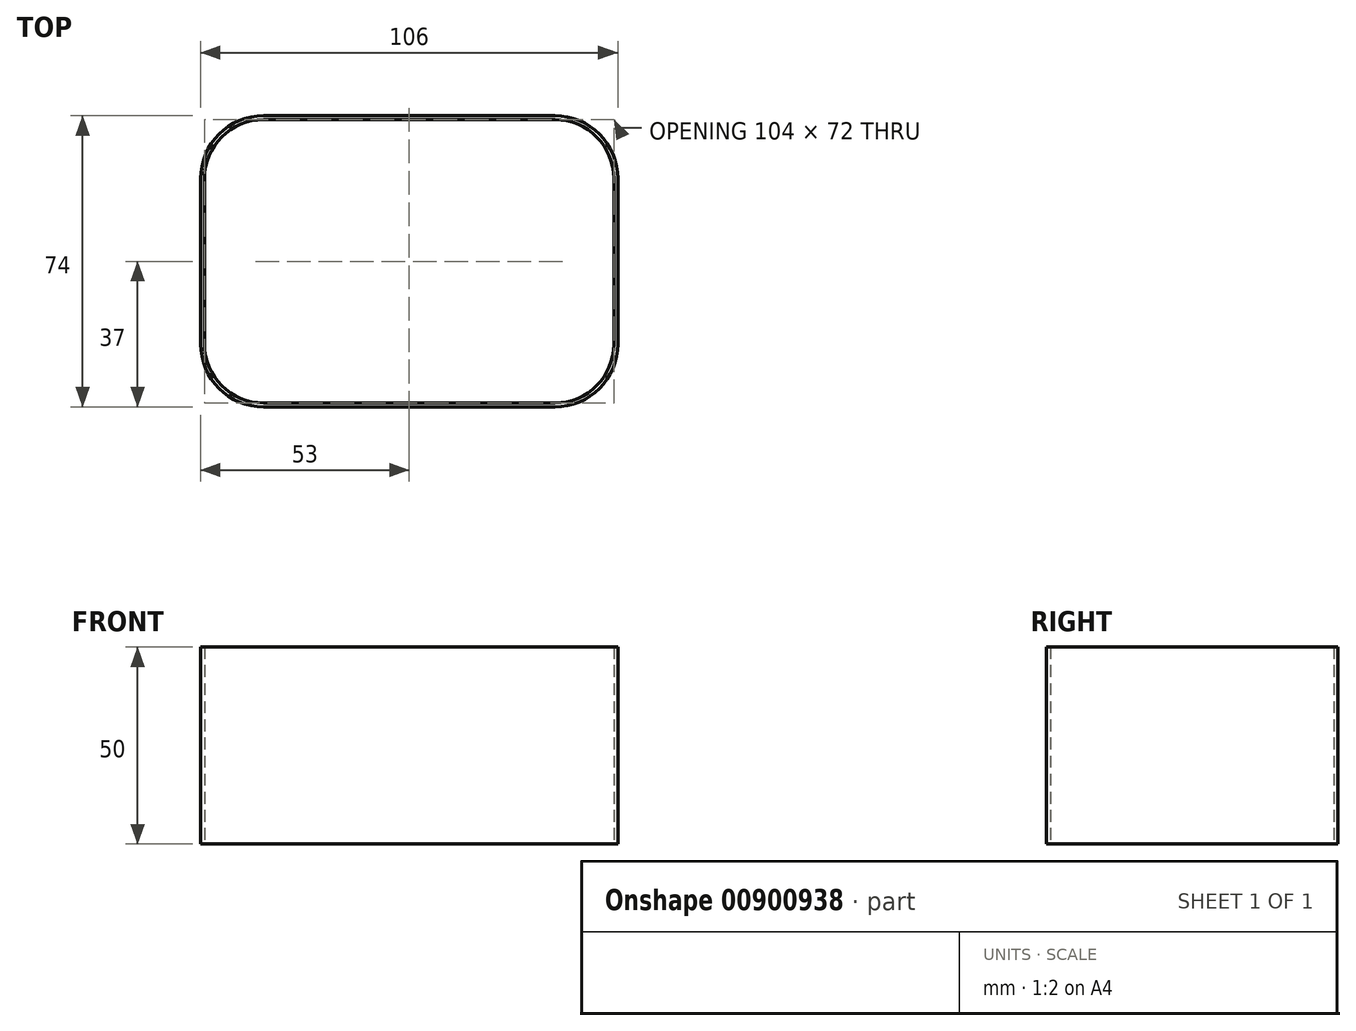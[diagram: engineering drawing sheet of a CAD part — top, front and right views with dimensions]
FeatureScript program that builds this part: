
annotation { "Feature Type Name" : "Feature", "Feature Type Description" : "" }
export const myFeature = defineFeature(function(context is Context, id is Id, definition is map)
    precondition{}
    {
        {
            var Q0;
            Q0=qCreatedBy(makeId("Top.planeOp"),FACE);
            var sketch = newSketch(context, id + "F0", { "sketchPlane" : qUnion([Q0])});
            skLineSegment(sketch, "E0.bottom", {"start": v(37, 37) * mm, "end": v(-37, 37) * mm});
            skLineSegment(sketch, "E0.top", {"start": v(37, -37) * mm, "end": v(-37, -37) * mm});
            skLineSegment(sketch, "E0.left", {"start": v(53, 21) * mm, "end": v(53, -21) * mm});
            skLineSegment(sketch, "E0.right", {"start": v(-53, 21) * mm, "end": v(-53, -21) * mm});
            skPoint(sketch, "E0.middle", {"position": v(0, 0) * mm});
            skPoint(sketch, "E1", {"position": v(37, 21) * mm});
            skArc(sketch, "E2", {"start": v(52, 21) * mm, "mid": v(47.6, 31.6) * mm, "end": v(37, 36) * mm});
            skArc(sketch, "E3", {"start": v(53, 21) * mm, "mid": v(48.31, 32.31) * mm, "end": v(37, 37) * mm});
            skLineSegment(sketch, "E4.trimOffspring", {"start": v(52, 21) * mm, "end": v(52, -21) * mm});
            skLineSegment(sketch, "E5.trimOffspring", {"start": v(37, 36) * mm, "end": v(-37, 36) * mm});
            skPoint(sketch, "E6.left.start.orphan", {"position": v(52, 36) * mm});
            skPoint(sketch, "E7.orphan", {"position": v(53, 37) * mm});
            skPoint(sketch, "E8", {"position": v(-37, -21) * mm});
            skArc(sketch, "E9", {"start": v(-52, -21) * mm, "mid": v(-47.6, -31.6) * mm, "end": v(-37, -36) * mm});
            skArc(sketch, "E10", {"start": v(-53, -21) * mm, "mid": v(-48.31, -32.31) * mm, "end": v(-37, -37) * mm});
            skPoint(sketch, "E11.orphan", {"position": v(-53, -37) * mm});
            skPoint(sketch, "E12.orphan", {"position": v(-52, -36) * mm});
            skPoint(sketch, "E13", {"position": v(-37, 21) * mm});
            skArc(sketch, "E14", {"start": v(-37, 36) * mm, "mid": v(-47.6, 31.6) * mm, "end": v(-52, 21) * mm});
            skArc(sketch, "E15", {"start": v(-37, 37) * mm, "mid": v(-48.31, 32.31) * mm, "end": v(-53, 21) * mm});
            skLineSegment(sketch, "E16.trimOffspring", {"start": v(-52, 21) * mm, "end": v(-52, -21) * mm});
            skPoint(sketch, "E17.orphan", {"position": v(-53, 37) * mm});
            skPoint(sketch, "E18.trimOffspring.end.orphan", {"position": v(-52, 36) * mm});
            skArc(sketch, "E19", {"start": v(37, -36) * mm, "mid": v(47.6, -31.6) * mm, "end": v(52, -21) * mm});
            skArc(sketch, "E20", {"start": v(37, -37) * mm, "mid": v(48.31, -32.31) * mm, "end": v(53, -21) * mm});
            skLineSegment(sketch, "E21.trimOffspring", {"start": v(37, -36) * mm, "end": v(-37, -36) * mm});
            skPoint(sketch, "E6.top.start.orphan", {"position": v(52, -36) * mm});
            skPoint(sketch, "E22.orphan", {"position": v(53, -37) * mm});
            skSolve(sketch);
        }
        {
            var Q0;
            Q0=qSketchRegion(id+"F0",true);
            extrude(context, id + "F1", {"entities" : qUnion([Q0]), "depth" : 50 * mm, "offsetDistance" : 25 * mm});
        }
    });
